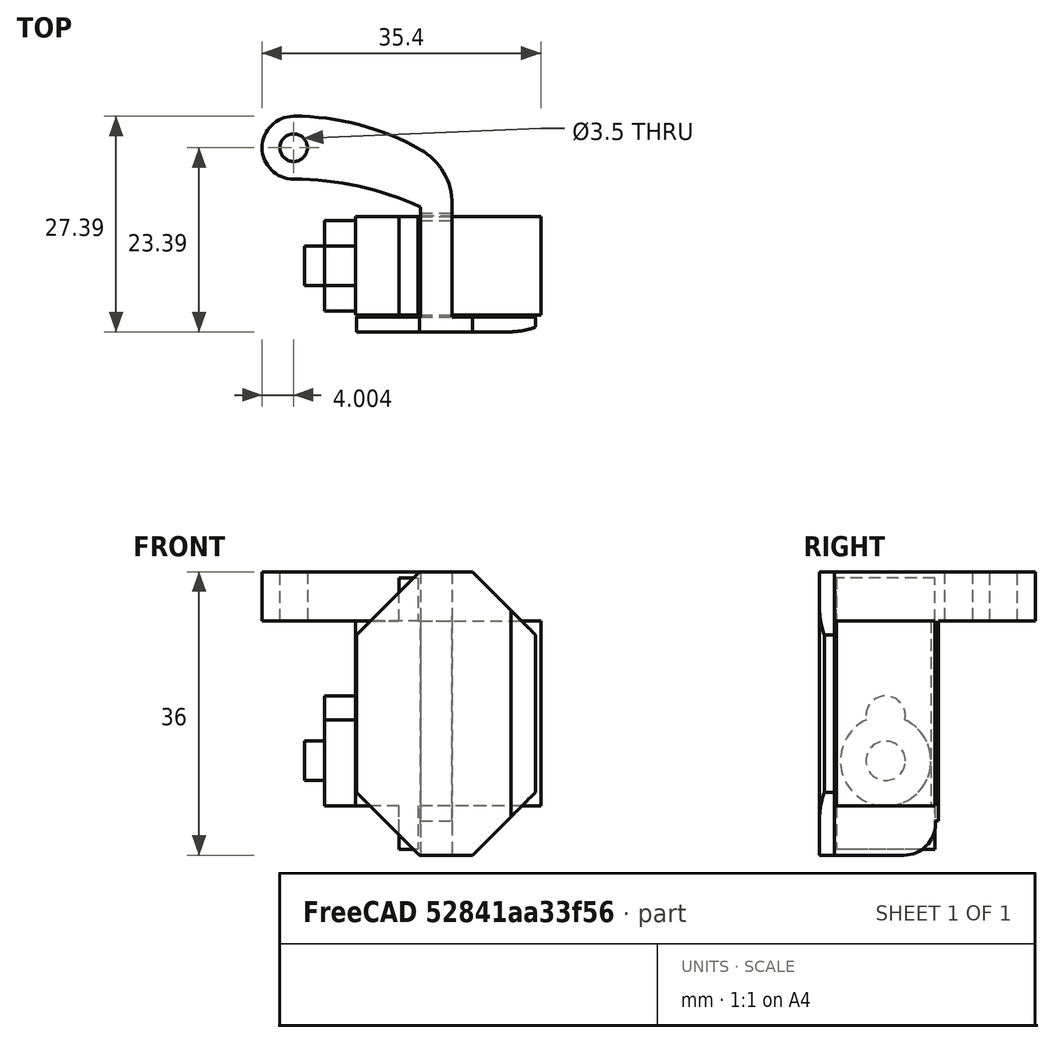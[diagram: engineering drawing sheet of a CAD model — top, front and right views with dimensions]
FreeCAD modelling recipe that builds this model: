
FCSTD DOCUMENT  (FreeCAD 0.20R29410 (Git))
Label: Fuse servo Mount
License: All rights reserved
LicenseURL: http://en.wikipedia.org/wiki/All_rights_reserved
objects: Sketcher::SketchObject×7, PartDesign::Pad×5, PartDesign::Body×2, PartDesign::Pocket×2, Mesh::Feature×2, PartDesign::Fillet×2, PartDesign::Chamfer×1
note: 29 computed .brp shape members not serialized (recipe doc carries the construction recipe); baked Part::Feature solids carry a one-line shape summary decoded from their .brp

FEATURE [Sketcher::SketchObject] Sketch056  label="Main Sketch"
  FullyConstrained = true
  MapMode = 5
  Placement = pos=(0,0,0) rot=(0.57735,0.57735,0.57735;2.0944rad)
  Support = -> [YZ_Plane010]
  expr: Constraints[34] = 23.5 / 2
  expr: Constraints[35] = 23.5 / 2
  sketch-geometry (12):
    g0: LineSegment StartX=-11.75 StartY=11.75 StartZ=0 EndX=3.85 EndY=11.75 EndZ=0
    g1: LineSegment StartX=3.85 StartY=11.75 StartZ=0 EndX=3.85 EndY=17.25 EndZ=0
    g2: LineSegment StartX=3.85 StartY=17.25 StartZ=0 EndX=6.25 EndY=17.25 EndZ=0
    g3: LineSegment StartX=6.25 StartY=17.25 StartZ=0 EndX=6.25 EndY=11.75 EndZ=0
    g4: LineSegment StartX=6.25 StartY=11.75 StartZ=0 EndX=11.75 EndY=11.75 EndZ=0
    g5: LineSegment StartX=11.75 StartY=11.75 StartZ=0 EndX=11.75 EndY=-11.75 EndZ=0
    g6: LineSegment StartX=11.75 StartY=-11.75 StartZ=0 EndX=6.25 EndY=-11.75 EndZ=0
    g7: LineSegment StartX=6.25 StartY=-11.75 StartZ=0 EndX=6.25 EndY=-17.25 EndZ=0
    g8: LineSegment StartX=6.25 StartY=-17.25 StartZ=0 EndX=3.85 EndY=-17.25 EndZ=0
    g9: LineSegment StartX=3.85 StartY=-17.25 StartZ=0 EndX=3.85 EndY=-11.75 EndZ=0
    g10: LineSegment StartX=3.85 StartY=-11.75 StartZ=0 EndX=-11.75 EndY=-11.75 EndZ=0
    g11: LineSegment StartX=-11.75 StartY=-11.75 StartZ=0 EndX=-11.75 EndY=11.75 EndZ=0
  constraints (36):
    c: Coincident(g0,g1)
    c: Coincident(g1,g2)
    c: Coincident(g2,g3)
    c: Coincident(g3,g4)
    c: Coincident(g4,g5)
    c: Vertical(g5)
    c: Coincident(g5,g6)
    c: Coincident(g6,g7)
    c: Coincident(g7,g8)
    c: Coincident(g8,g9)
    c: Coincident(g9,g10)
    c: Coincident(g10,g11)
    c: Coincident(g11,g0)
    c: Vertical(g11)
    c: Horizontal(g0,g0)
    c: Horizontal(g0,g3)
    c: Horizontal(g3,g4)
    c: Horizontal(g10,g9)
    c: Horizontal(g9,g6)
    c: Horizontal(g6,g5)
    c: Vertical(g9,g0)
    c: Vertical(g0,g1)
    c: Vertical(g1,g8)
    c: Vertical(g7,g6)
    c: Vertical(g6,g3)
    c: Vertical(g3,g2)
    c: Horizontal(g8)
    c: Horizontal(g2)
    c: DistanceX(g2,g2) = 2.4
    c: DistanceX(g0,g4) = 23.5
    c: DistanceX(g4,g4) = 5.5
    c: DistanceY(g11,g11) = 23.5
    c: DistanceY(g1,g1) = 5.5
    c: Equal(g9,g1)
    c: DistanceY(g-1,g0) = 11.75
    c: DistanceX(g0,g-1) = 11.75
FEATURE [PartDesign::Pad] Pad004  label="Body Pad"
  Direction = (1,1,1)
  Length = 12.5
  Length2 = 100
  Midplane = true
  Placement = pos=(0,0,0) rot=(0.57735,0.57735,0.57735;2.0944rad)
  Profile = -> Sketch056
  Type = 0
FEATURE [Sketcher::SketchObject] Sketch057
  ExternalGeometry = -> [Pad004]
  FullyConstrained = true
  MapMode = 5
  Placement = pos=(5.2e-15,11.75,-2.6e-15) rot=(0.57735,0.57735,0.57735;4.18879rad)
  Support = -> [Pad004]
  expr: Constraints[2] = 11.5 / 2
  sketch-geometry (2):
    g0: ArcOfCircle CenterX=6 CenterY=0 CenterZ=0 NormalX=0 NormalY=0 NormalZ=1 AngleXU=0 Radius=5.75 StartAngle=3.57987 EndAngle=8.9865
    g1: ArcOfCircle CenterX=0.25 CenterY=0 CenterZ=0 NormalX=0 NormalY=0 NormalZ=1 AngleXU=0 Radius=2.5 StartAngle=1.35166 EndAngle=4.93153
  constraints (8):
    c: PointOnObject(g0,g-1)
    c: Diameter(g0) = 11.5
    c: DistanceX(g0,g-3) = 5.75
    c: PointOnObject(g1,g-1)
    c: Diameter(g1) = 5
    c: DistanceX(g1,g-3) = 11.5
    c: Coincident(g0,g1)
    c: Coincident(g0,g1)
FEATURE [PartDesign::Pad] Pad005  label="Head1"
  BaseFeature = -> Pad004
  Direction = (1,1,1)
  Length = 4
  Length2 = 100
  Placement = pos=(0,0,0) rot=(0.57735,0.57735,0.57735;2.0944rad)
  Profile = -> Sketch057
  Type = 0
FEATURE [Sketcher::SketchObject] Sketch058
  ExternalGeometry = -> [Pad005]
  FullyConstrained = true
  MapMode = 5
  Placement = pos=(7.1e-15,15.75,-3.5e-15) rot=(0.57735,0.57735,0.57735;4.18879rad)
  Support = -> [Pad005]
  sketch-geometry (1):
    g0: Circle CenterX=6 CenterY=0 CenterZ=0 NormalX=0 NormalY=0 NormalZ=1 AngleXU=0 Radius=2.5
  constraints (2):
    c: Coincident(g0,g-3)
    c: Diameter(g0) = 5
FEATURE [PartDesign::Pad] Pad006  label="Splines"
  BaseFeature = -> Pad005
  Direction = (1,1,1)
  Length = 2.5
  Length2 = 100
  Placement = pos=(0,0,0) rot=(0.57735,0.57735,0.57735;2.0944rad)
  Profile = -> Sketch058
  Type = 0
FEATURE [PartDesign::Body] Body010  label="Servo"
  Group = -> [Sketch056,Pad004,Sketch057,Pad005,Sketch058,Pad006]
  Origin = -> Origin010
  Placement = pos=(126,-22,111) rot=(-0.707107,0.707107,0;3.14159rad)
  Tip = -> Pad006
FEATURE [Sketcher::SketchObject] Sketch
  FullyConstrained = false
  MapMode = 5
  Support = -> [XY_Plane]
  sketch-geometry (11):
    g0: Circle CenterX=-90.646 CenterY=20 CenterZ=0 NormalX=0 NormalY=0 NormalZ=1 AngleXU=0 Radius=1.75
    g1: ArcOfCircle CenterX=-90.646 CenterY=20 CenterZ=0 NormalX=0 NormalY=0 NormalZ=1 AngleXU=0 Radius=4 StartAngle=1.5708 EndAngle=4.71239
    g2: LineSegment StartX=-82.646 StartY=-1.52958 StartZ=0 EndX=-74.496 EndY=-1.52958 EndZ=0
    g3: LineSegment StartX=-59.9244 StartY=-1.48465 StartZ=0 EndX=-59.9244 EndY=-5.94813 EndZ=0
    g4: LineSegment StartX=-59.9244 StartY=-5.94813 StartZ=0 EndX=-82.646 EndY=-5.94813 EndZ=0
    g5: LineSegment StartX=-82.646 StartY=-5.94813 StartZ=0 EndX=-82.646 EndY=-1.52958 EndZ=0
    g6: LineSegment StartX=-70.496 StartY=17.067 StartZ=0 EndX=-70.496 EndY=-1.48465 EndZ=0
    g7: LineSegment StartX=-74.496 StartY=-1.52958 StartZ=0 EndX=-74.496 EndY=12.4758 EndZ=0
    g8: ArcOfCircle CenterX=-90.646 CenterY=-8.74821 CenterZ=0 NormalX=0 NormalY=0 NormalZ=1 AngleXU=0 Radius=32.7482 StartAngle=0.908029 EndAngle=1.5708
    g9: ArcOfCircle CenterX=-90.646 CenterY=-22.7662 CenterZ=0 NormalX=0 NormalY=0 NormalZ=1 AngleXU=0 Radius=38.7662 StartAngle=1.14109 EndAngle=1.5708
    g10: LineSegment StartX=-70.496 StartY=-1.48465 StartZ=0 EndX=-59.9244 EndY=-1.48465 EndZ=0
  constraints (27):
    c: Coincident(g1,g0)
    c: Coincident(g10,g3)
    c: Coincident(g3,g4)
    c: Coincident(g4,g5)
    c: Coincident(g5,g2)
    c: Horizontal(g2)
    c: Horizontal(g4)
    c: Vertical(g3)
    c: Vertical(g5)
    c: Vertical(g6)
    c: Vertical(g7)
    c: Coincident(g7,g9)
    c: Tangent(g1,g9) = 1.5708
    c: Tangent(g1,g8) = -1.5708
    c: Coincident(g2,g7)
    c: Coincident(g10,g6)
    c: Vertical(g1,g0)
    c: Vertical(g0,g1)
    c: Coincident(g8,g6)
    c: DistanceX(g2,g6) = 4
    c: DistanceX(g2,g2) = 8.15
    c: DistanceX(g2) = -82.646
    c: DistanceY(g2) = -1.52958
    c: DistanceX(g0,g2) = 8
    c: Diameter(g0) = 3.5
    c: DistanceY(g0) = 20
    c: Diameter(g1) = 8
FEATURE [PartDesign::Pad] Pad
  Direction = (0,0,1)
  Length = 36
  Length2 = 10
  Profile = -> Sketch
  ReferenceAxis = -> Sketch [N_Axis]
  Reversed = true
  Type = 0
FEATURE [Sketcher::SketchObject] Sketch059
  AttachmentOffset = pos=(0,0,-106) rot=(0,0,1;0rad)
  ExternalGeometry = -> [Pad]
  FullyConstrained = false
  MapMode = 5
  Placement = pos=(-106,2.35e-14,-2.35e-14) rot=(0.57735,0.57735,0.57735;2.0944rad)
  Support = -> [YZ_Plane]
  sketch-geometry (6):
    g0: LineSegment StartX=-1.48465 StartY=-6.23129 StartZ=0 EndX=33.8255 EndY=-6.23129 EndZ=0
    g1: LineSegment StartX=11.3154 StartY=-29.6808 StartZ=0 EndX=-1.48465 EndY=-29.6808 EndZ=0
    g2: LineSegment StartX=-1.48465 StartY=-29.6808 StartZ=0 EndX=-1.48465 EndY=-6.23129 EndZ=0
    g3: LineSegment StartX=11.3154 StartY=-29.6808 StartZ=0 EndX=11.3154 EndY=-48.6212 EndZ=0
    g4: LineSegment StartX=11.3154 StartY=-48.6212 StartZ=0 EndX=33.8255 EndY=-48.6212 EndZ=0
    g5: LineSegment StartX=33.8255 StartY=-6.23129 StartZ=0 EndX=33.8255 EndY=-48.6212 EndZ=0
  constraints (14):
    c: Coincident(g1,g2)
    c: Coincident(g2,g0)
    c: Horizontal(g0)
    c: Horizontal(g1)
    c: Vertical(g2)
    c: PointOnObject(g0,g-3)
    c: Coincident(g3,g4)
    c: Horizontal(g4)
    c: Vertical(g3)
    c: DistanceX(g1,g1) = 12.8
    c: Coincident(g1,g3)
    c: Coincident(g5,g0)
    c: Coincident(g5,g4)
    c: Vertical(g5)
FEATURE [PartDesign::Pocket] Pocket
  BaseFeature = -> Pad
  Direction = (-1,2e-16,-3e-16)
  Length = 5
  Length2 = 5
  Profile = -> Sketch059
  ReferenceAxis = -> Sketch059 [N_Axis]
  Reversed = true
  Type = 1
FEATURE [PartDesign::Chamfer] Chamfer
  Angle = 45
  Base = -> Pocket [Edge32,Edge9,Edge11,Edge38]
  BaseFeature = -> Pocket
  ChamferType = 0
  FlipDirection = false
  Size = 8
  Size2 = 1
  SupportTransform = false
  UseAllEdges = false
FEATURE [Mesh::Feature] Ta152_fuselage_3  label="Ta152 fuselage 3"
FEATURE [Sketcher::SketchObject] Sketch060
  AttachmentOffset = pos=(0,-1,0) rot=(0,0,1;0rad)
  FullyConstrained = false
  MapMode = 5
  Placement = pos=(0,1,-36) rot=(1,0,0;3.14159rad)
  Support = -> [Chamfer]
  sketch-geometry (6):
    g0: LineSegment StartX=-83.7369 StartY=4.39442 StartZ=0 EndX=-63.0555 EndY=4.39442 EndZ=0
    g1: ArcOfCircle CenterX=-63.3036 CenterY=-5.30116 CenterZ=0 NormalX=0 NormalY=0 NormalZ=1 AngleXU=0 Radius=9.69875 StartAngle=0.292818 EndAngle=1.54522
    g2: LineSegment StartX=-83.7369 StartY=4.39442 StartZ=0 EndX=-83.7369 EndY=7.74094 EndZ=0
    g3: LineSegment StartX=-83.7369 StartY=7.74094 StartZ=0 EndX=-53.116 EndY=7.74094 EndZ=0
    g4: LineSegment StartX=-53.116 StartY=7.74094 StartZ=0 EndX=-53.116 EndY=-2.69274 EndZ=0
    g5: LineSegment StartX=-53.116 StartY=-2.69274 StartZ=0 EndX=-54.0177 EndY=-2.5016 EndZ=0
  constraints (12):
    c: Horizontal(g0)
    c: Coincident(g1,g0)
    c: DistanceX(g0) = -63.0555
    c: DistanceY(g0) = 4.39442
    c: Coincident(g2,g0)
    c: Vertical(g2)
    c: Coincident(g2,g3)
    c: Horizontal(g3)
    c: Coincident(g3,g4)
    c: Vertical(g4)
    c: Coincident(g4,g5)
    c: Coincident(g5,g1)
FEATURE [PartDesign::Pocket] Pocket001
  BaseFeature = -> Chamfer
  Direction = (0,0,1)
  Length = 5
  Length2 = 5
  Profile = -> Sketch060
  ReferenceAxis = -> Sketch060 [N_Axis]
  Type = 1
FEATURE [Sketcher::SketchObject] Sketch061
  ExternalGeometry = -> [Pocket001]
  FullyConstrained = false
  MapMode = 5
  Placement = pos=(-74.496,0,0) rot=(0.57735,-0.57735,-0.57735;2.0944rad)
  Support = -> [Pocket001]
  sketch-geometry (4):
    g0: LineSegment StartX=-10.7154 StartY=-31.6152 StartZ=0 EndX=-11.7154 EndY=-31.6152 EndZ=0
    g1: LineSegment StartX=-11.7154 StartY=-31.6152 StartZ=0 EndX=-11.7154 EndY=-5.61483 EndZ=0
    g2: LineSegment StartX=-11.7154 StartY=-5.61483 StartZ=0 EndX=-10.7154 EndY=-5.61483 EndZ=0
    g3: LineSegment StartX=-10.7154 StartY=-5.61483 StartZ=0 EndX=-10.7154 EndY=-31.6152 EndZ=0
  constraints (10):
    c: Coincident(g0,g1)
    c: Coincident(g1,g2)
    c: Coincident(g2,g3)
    c: Coincident(g3,g0)
    c: Horizontal(g0)
    c: Horizontal(g2)
    c: Vertical(g1)
    c: Vertical(g3)
    c: DistanceX(g-3,g0) = 0.6
    c: DistanceX(g0,g0) = 1
FEATURE [PartDesign::Pad] Pad007
  BaseFeature = -> Pocket001
  Direction = (-1,0,0)
  Length = 4
  Length2 = 10
  Profile = -> Sketch061
  ReferenceAxis = -> Sketch061 [N_Axis]
  Reversed = true
  Type = 0
FEATURE [PartDesign::Fillet] Fillet
  Base = -> Pad007 [Edge34]
  BaseFeature = -> Pad007
  Radius = 8
  SupportTransform = false
  UseAllEdges = false
FEATURE [PartDesign::Fillet] Fillet001
  Base = -> Fillet [Edge73]
  BaseFeature = -> Fillet
  Radius = 4
  SupportTransform = false
  UseAllEdges = false
FEATURE [PartDesign::Body] Body  label="Servo Holder"
  Group = -> [Sketch,Pad,Sketch059,Pocket,Chamfer,Sketch060,Pocket001,Sketch061,Pad007,Fillet,Fillet001]
  Origin = -> Origin
  Placement = pos=(197,-27,129) rot=(0,0,1;0rad)
  Tip = -> Fillet001
FEATURE [Mesh::Feature] Mesh  label="Servo Holder (Meshed)"
